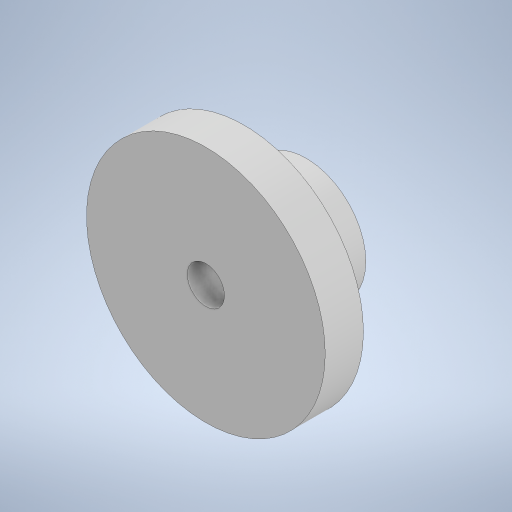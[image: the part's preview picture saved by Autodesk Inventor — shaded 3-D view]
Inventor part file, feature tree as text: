
AUTODESK INVENTOR PART (.ipt)
format: ipt  version: 2023 (Build 270158000, 158)  size: 240,640 bytes
history: native  units: in
note: dims shown in document units (in); Inventor stores cm internally (conversion verified against a paired STEP export)
features: extrude x3, sketch x2
ambient origin geometry x8: Origin, YZ Plane, XZ Plane, XY Plane, X Axis, Y Axis, Z Axis, Center Point
bodies: Solid1 (feature_tree)
feature tree (5):
  sketch  "Sketch1"  dims[d0=0.5in d1=0.25in]
  extrude  "Extrusion1"  Depth=0.25in
  extrude  "Extrusion2"  Depth=0.13in TaperAngle=0.0deg
  extrude  "Extrusion3"  Depth=0.13in TaperAngle=0.0deg
  sketch  "Sketch2"  dims[d2=0.0781in d3=0.08in d4=0.0in d5=0.13in d6=0.0in d7=0.056in d8=0.065in d9=0.13in d10=0.0in]
